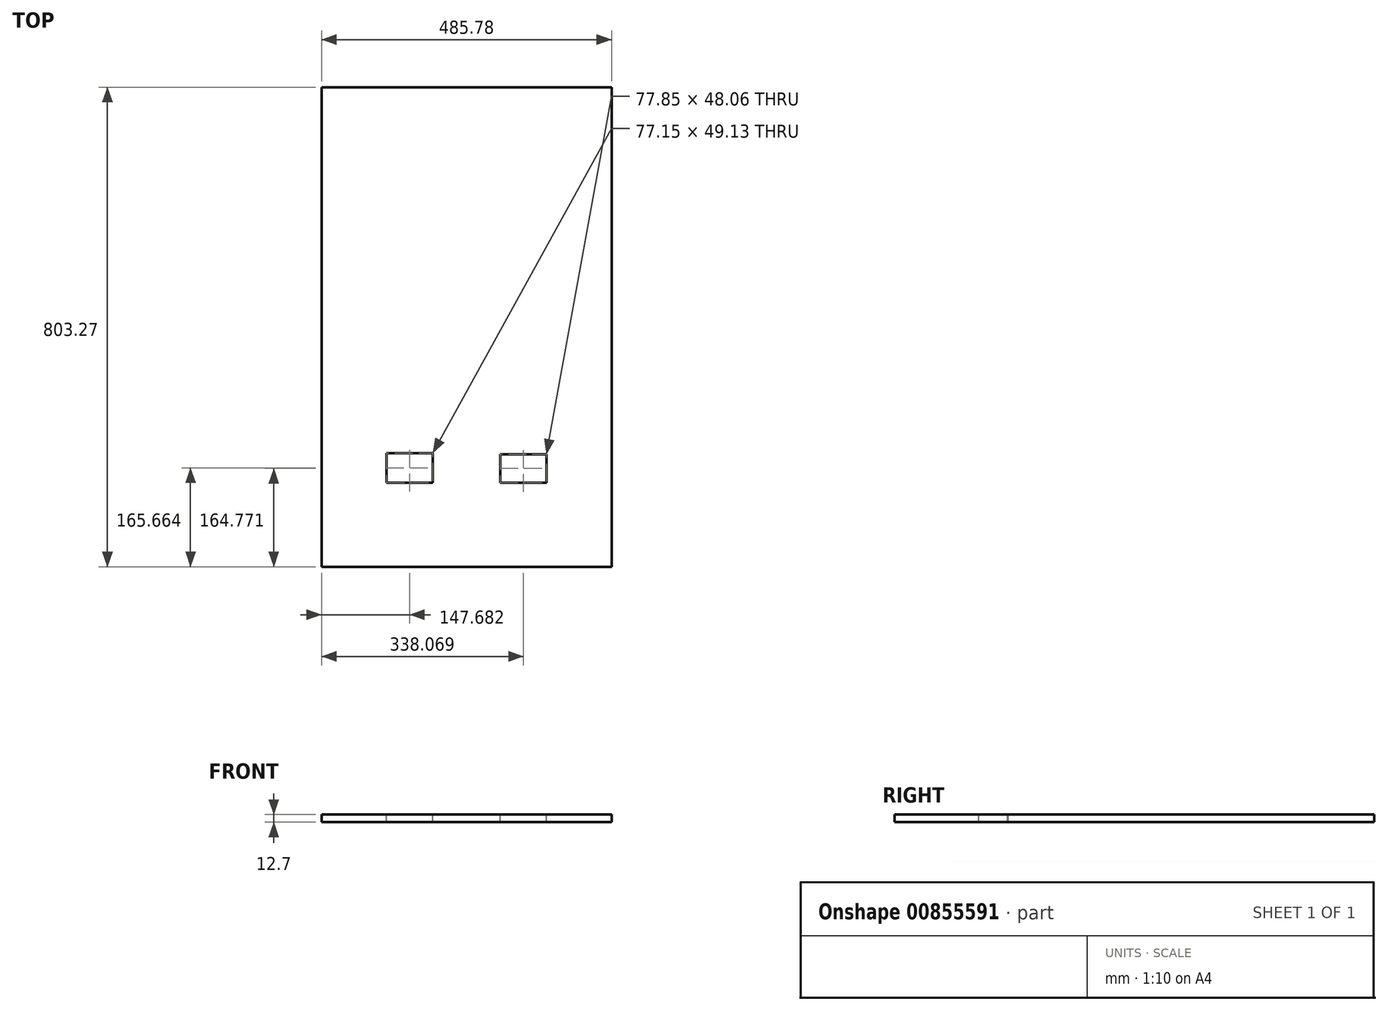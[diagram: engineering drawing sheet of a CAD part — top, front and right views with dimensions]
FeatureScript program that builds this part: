
annotation { "Feature Type Name" : "Feature", "Feature Type Description" : "" }
export const myFeature = defineFeature(function(context is Context, id is Id, definition is map)
    precondition{}
    {
        {
            var Q0;
            Q0=qCreatedBy(makeId("Top.planeOp"),FACE);
            var sketch = newSketch(context, id + "F0", { "sketchPlane" : qUnion([Q0])});
            skLineSegment(sketch, "E0.bottom", {"start": v(0, 0) * mm, "end": v(485.78, 0) * mm});
            skLineSegment(sketch, "E0.top", {"start": v(0, 803.27) * mm, "end": v(485.77, 803.27) * mm});
            skLineSegment(sketch, "E0.left", {"start": v(0, 0) * mm, "end": v(0, 803.27) * mm});
            skLineSegment(sketch, "E0.right", {"start": v(485.78, 0) * mm, "end": v(485.78, 803.27) * mm});
            skSolve(sketch);
        }
        {
            var Q0;
            Q0=qSketchRegion(id+"F0",true);
            extrude(context, id + "F1", {"entities" : qUnion([Q0]), "depth" : 12.7 * mm, "offsetDistance" : 25.4 * mm});
        }
        {
            var Q0;
            Q0=makeQuery(id+"F1.opExtrude","CAP_FACE",FACE,{"disambiguationData":[OSD([sQuery(id+"F0.wireOp",EDGE,"E0.bottom"),sQuery(id+"F0.wireOp",EDGE,"E0.top"),sQuery(id+"F0.wireOp",EDGE,"E0.left"),sQuery(id+"F0.wireOp",EDGE,"E0.right")])],"isStart":false});
            var sketch = newSketch(context, id + "F2", { "sketchPlane" : qUnion([Q0])});
            skLineSegment(sketch, "E1.bottom", {"start": v(109.1, 190.23) * mm, "end": v(186.26, 190.23) * mm});
            skLineSegment(sketch, "E1.top", {"start": v(109.1, 141.1) * mm, "end": v(186.26, 141.1) * mm});
            skLineSegment(sketch, "E1.left", {"start": v(109.1, 190.23) * mm, "end": v(109.1, 141.1) * mm});
            skLineSegment(sketch, "E1.right", {"start": v(186.26, 190.23) * mm, "end": v(186.26, 141.1) * mm});
            skLineSegment(sketch, "E2.bottom", {"start": v(299.14, 188.8) * mm, "end": v(377, 188.8) * mm});
            skLineSegment(sketch, "E2.top", {"start": v(299.14, 140.74) * mm, "end": v(377, 140.74) * mm});
            skLineSegment(sketch, "E2.left", {"start": v(299.14, 188.8) * mm, "end": v(299.14, 140.74) * mm});
            skLineSegment(sketch, "E2.right", {"start": v(377, 188.8) * mm, "end": v(377, 140.74) * mm});
            skSolve(sketch);
        }
        {
            var Q0;
            Q0=qSketchRegion(id+"F2",true);
            extrude(context, id + "F3", {"entities" : qUnion([Q0]), "operationType" : NewBodyOperationType.REMOVE, "oppositeDirection" : true, "depth" : 25.4 * mm, "offsetDistance" : 25.4 * mm});
        }
    });
